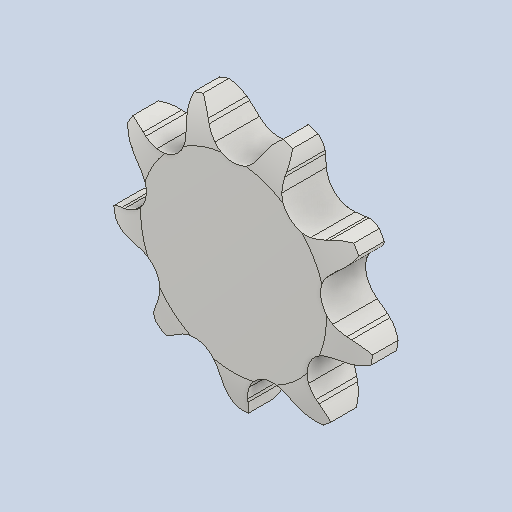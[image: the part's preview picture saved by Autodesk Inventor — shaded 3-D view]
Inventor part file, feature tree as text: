
AUTODESK INVENTOR PART (.ipt)
format: ipt  version: 2022.1 (Build 261234000, 234)  size: 374,784 bytes
history: native  units: mm
features: other x6, extrude x2, pattern_linear x1, pattern_circular x1
ambient origin geometry x8: Origin, YZ Plane, XZ Plane, XY Plane, X Axis, Y Axis, Z Axis, Center Point
bodies: Solid1 (feature_tree)
feature tree (10):
  other  "Perfil de diente teórico"
  other  "Perfil de diente"
  other  "Perfil de sección"
  other  "Cubierta"
  other  "Ramal"
  pattern_linear  "Patrón de ramal"  Spacing1=46.415395mm  [1 undecoded]
  extrude  "Diente teórico"  Depth=6.981317mm
  extrude  "Diente"  Depth=5.1308mm
  pattern_circular  "Patrón de diente"  [2 undecoded]
  other  "Plano síncrono"
note: 3 required parameter values undecoded (feature->parameter linkage not recoverable at this tier; creation-order binding heuristic only, values carry confidence <= 0.55)
